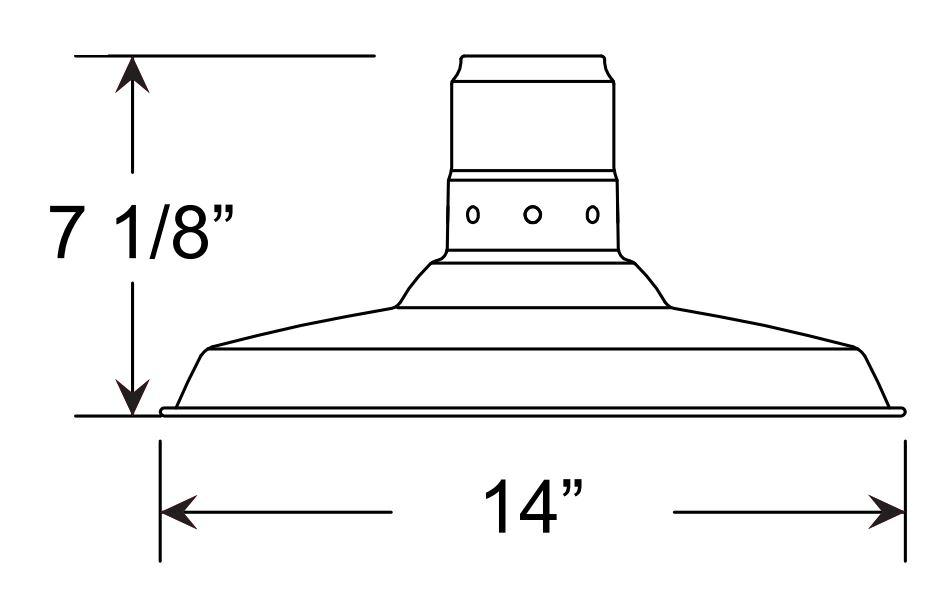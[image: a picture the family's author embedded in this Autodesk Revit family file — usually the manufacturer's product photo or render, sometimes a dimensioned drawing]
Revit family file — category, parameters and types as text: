
# Revit family: Orbitor 100w -12,16 MB
name_source: partatom
category: Lighting Fixtures
units: mm (PartAtom-declared; Revit-internal decimal feet)

## family parameters
Always vertical = Yes
Cut with Voids When Loaded = No
Light Source = Yes
OmniClass Number = 23.80.70.00
OmniClass Title = Lighting
Part Type = Normal
Room Calculation Point = No
Round Connector Dimension = Use Diameter
Shared = No
Work Plane-Based = No

## types (2) — shared parameters
Body Colour = Spun aluminium
Body Material = body
CRI = >90
Color Filter = 16777215
Construction Material = Heavy Duty spun aluminum.
Default Elevation = 0' - 0"
Description = 120-277 Voltage
Dimming = 1%
Dimming Lamp Color Temperature Shift = <None>
Efficiency = 65-125 lumens per watt
INSIDE BODY = INSIDE BODY
Lamp = MB
Life = L70 50,000 hours
Load Classification = Lighting
Manufacturer = ANP Lighting
Photometric Web File = generic.ies
Power Factor = 1
Tilt Angle = 90.00°
URL = https://www.anplighting.com
Voltage = 277 V
Warranty = 5 year limited warranty
Wattage Comments = 100W Max
Weight = 2.0 lbs

## per-type parameters (varying)
| type | Apparent Load | Fixture Diameter | Fixture Height | ORBT12 | ORBT16 |
| ORBT12 | 200 VA | 1' - 0" | 0' - 11 1/2" | Yes | No |
| ORBT16 | 100 VA | 1' - 4" | 1' - 0" | No | Yes |

note: column(s) folded — value = type name in every type: Model

## geometry (parser evidence)
native form markers: Sweep x26
no freeform markers — native parametric forms only
